# Revit family: BENCH_CANTILEVER
name_source: partatom
category: Furniture
units: mm (PartAtom-declared; Revit-internal decimal feet)

## family parameters
Always vertical = Yes
Cut with Voids When Loaded = No
OmniClass Number = 23.40.20.00
OmniClass Title = General Furniture and Specialties
Room Calculation Point = No
Shared = No
Work Plane-Based = No

## types (12) — shared parameters
FULL_WT = Yes
Manufacturer = IBR InnovaSystem
WT_12-75_XL = No
WT_15-75 = No
WT_15-75_XL = No
WT_6-75_XL = No
WT_9-75_XL = No
XL_WORKTOP = No
midleg = No
zero-valued in all types: Default Elevation

## per-type parameters (varying)
| type | Description | HEIGHT | LOW_TAG | Length | URL | WT_12-75 | WT_6-75 | WT_9-75 | depth |
| CNB-12759 | Cantilever Bench 1200x750x900 | 900 mm  [stored 2.95276 ft] | No | 1200 mm  [stored 3.93701 ft] | https://ibr-innovasystem.com | Yes | No | No | 750 mm  [stored 2.46063 ft] |
| CNB-12609 | Cantilever Bench 1200x600x900 | 900 mm  [stored 2.95276 ft] | No | 1200 mm  [stored 3.93701 ft] | https://ibr-innovasystem.com | Yes | No | No | 600 mm |
| CNB-12757 | Cantilever Bench 1200x750x750 | 750 mm  [stored 2.46063 ft] | Yes | 1200 mm  [stored 3.93701 ft] | https://ibr-innovasystem.com | Yes | No | No | 750 mm  [stored 2.46063 ft] |
| CNB-12607 | Cantilever Bench 1200x600x750 | 750 mm  [stored 2.46063 ft] | Yes | 1200 mm  [stored 3.93701 ft] | https://ibr-innovasystem.com | Yes | No | No | 600 mm |
| CNB-09759 | Cantilever Bench 900x750x900 | 900 mm  [stored 2.95276 ft] | No | 900 mm  [stored 2.95276 ft] | https://ibr-innovasystem.com | No | No | Yes | 750 mm  [stored 2.46063 ft] |
| CNB-09609 | Cantilever Bench 900x600x900 | 900 mm  [stored 2.95276 ft] | No | 900 mm  [stored 2.95276 ft] | https://ibr-innovasystem.com | No | No | Yes | 600 mm |
| CNB-09757 | Cantilever Bench 900x750x750 | 750 mm  [stored 2.46063 ft] | Yes | 900 mm  [stored 2.95276 ft] | https://ibr-innovasystem.com | No | No | Yes | 750 mm  [stored 2.46063 ft] |
| CNB-09607 | Cantilever Bench 900x600x750 | 750 mm  [stored 2.46063 ft] | Yes | 900 mm  [stored 2.95276 ft] | https://ibr-innovasystem.com | No | No | Yes | 600 mm |
| CNB-06759 | Cantilever Bench 600x750x900 | 900 mm  [stored 2.95276 ft] | No | 600 mm | https://ibr-innovasystem.com | No | Yes | No | 750 mm  [stored 2.46063 ft] |
| CNB-06609 | Cantilever Bench 600x600x900 | 900 mm  [stored 2.95276 ft] | No | 600 mm | https://ibr-innovasystem.com | No | Yes | No | 600 mm |
| CNB-06757 | Cantilever Bench 600x750x750 | 750 mm  [stored 2.46063 ft] | Yes | 600 mm | https://ibr-innovasystem.com | No | Yes | No | 750 mm  [stored 2.46063 ft] |
| CNB-06607 | Cantilever Bench 600x600x750 | 750 mm  [stored 2.46063 ft] | Yes | 600 mm | https://ibr-innovasystem.com
https://ibr-innovasystem.com | No | Yes | No | 600 mm |

note: [stored X ft] marks values corroborated as IEEE doubles in the binary element streams (Revit-internal decimal feet)

## geometry (parser evidence)
native form markers: Sweep x14
no freeform markers — native parametric forms only
